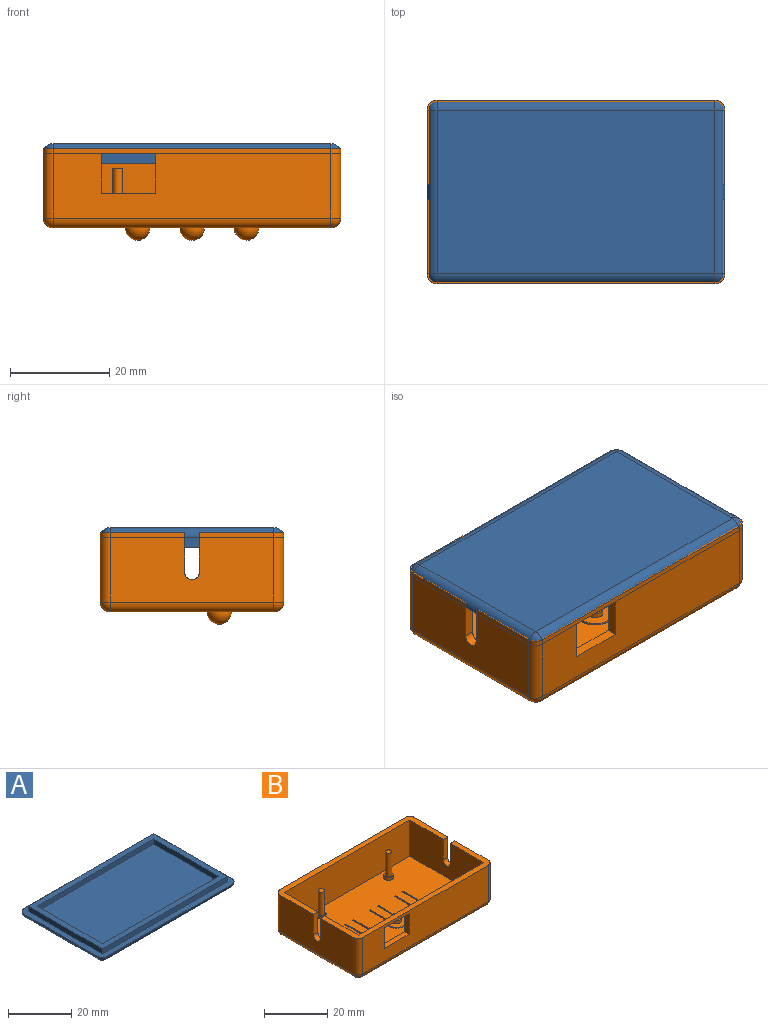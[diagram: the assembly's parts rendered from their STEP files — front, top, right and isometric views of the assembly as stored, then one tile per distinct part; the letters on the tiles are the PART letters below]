
ASSEMBLY  parts=2 mates=1
PART A: 20 faces, bbox 60x37x4 mm
  f0: plane 56x33mm, normal (0,0,1), area 340mm2, adj f3,f4,f5,f6,f8,f9,f10,f11
  f1: plane 60x37mm, normal (0,0,1), area 368.6mm2, adj f3,f4,f5,f6,f12,f13,f14,f15
  f2: plane 56x33mm, normal (0,0,-1), area 1848mm2, adj f13,f14,f17,f18
  f3: plane 33x2mm, normal (-1,0,0), area 66mm2, adj f0,f1,f4,f6
  f4: plane 56x2mm, normal (0,-1,0), area 112mm2, adj f0,f1,f3,f5
  f5: plane 33x2mm, normal (1,0,0), area 66mm2, adj f0,f1,f4,f6
  f6: plane 56x2mm, normal (0,1,0), area 112mm2, adj f0,f1,f3,f5
  f7: plane 52x29mm, normal (0,0,1), area 1508mm2, adj f8,f9,f10,f11
  f8: plane 29x2mm, normal (1,0,0), area 58mm2, adj f0,f7,f9,f11
  f9: plane 52x2mm, normal (0,1,0), area 104mm2, adj f0,f7,f8,f10
  f10: plane 29x2mm, normal (-1,0,0), area 58mm2, adj f0,f7,f9,f11
  f11: plane 52x2mm, normal (0,-1,0), area 104mm2, adj f0,f7,f8,f10
  f12: sphere r=2mm, area 6.3mm2, adj f1,f13,f14
  f13: cylinder r=2mm len=33mm, axis (0,1,0), area 103.7mm2, adj f1,f2,f12,f15
  f14: cylinder r=2mm len=56mm, axis (-1,0,0), area 175.9mm2, adj f1,f2,f12,f16
  f15: sphere r=2mm, area 6.3mm2, adj f1,f13,f17
  f16: sphere r=2mm, area 6.3mm2, adj f1,f14,f18
  f17: cylinder r=2mm len=56mm, axis (1,0,0), area 175.9mm2, adj f1,f2,f15,f19
  f18: cylinder r=2mm len=33mm, axis (0,-1,0), area 103.7mm2, adj f1,f2,f16,f19
  f19: sphere r=2mm, area 6.3mm2, adj f1,f17,f18
PART B: 79 faces, bbox 60x37x18.5 mm
  f0: plane 56x33mm, normal (0,0,1), area 1755.7mm2, adj f3,f9,f10,f11,f34,f35,f36,f37
  f1: plane 56x33mm, normal (0,0,-1), area 1739.2mm2, adj f15,f16,f20,f21,f34,f35,f36,f37
  f2: plane 56x14mm, normal (0,-1,0), area 696mm2, adj f7,f14,f20,f23,f30,f31,f32,f33
  f3: plane 56x14mm, normal (0,1,0), area 696mm2, adj f0,f7,f9,f10,f30,f31,f32,f33
  f4: plane 60x17mm, normal (0,0,1), area 178.3mm2, adj f5,f6,f8,f9,f10,f11,f12,f17
  f5: plane 33x14mm, normal (-1,0,0), area 434.5mm2, adj f4,f7,f17,f21,f23,f27,f28,f29
  f6: plane 33x14mm, normal (1,0,0), area 434.5mm2, adj f4,f7,f12,f14,f15,f24,f25,f26
  f7: plane 60x17mm, normal (0,0,1), area 178.3mm2, adj f2,f3,f5,f6,f9,f10,f14,f23
  f8: plane 56x14mm, normal (0,1,0), area 784mm2, adj f4,f12,f16,f17
  f9: plane 33x14mm, normal (1,0,0), area 434.5mm2, adj f0,f3,f4,f7,f11,f27,f28,f29
  f10: plane 33x14mm, normal (-1,0,0), area 434.5mm2, adj f0,f3,f4,f7,f11,f24,f25,f26
  f11: plane 56x14mm, normal (0,-1,0), area 784mm2, adj f0,f4,f9,f10
  f12: cylinder r=2mm len=14mm, axis (0,0,1), area 44mm2, adj f4,f6,f8,f13
  f13: sphere r=2mm, area 6.3mm2, adj f12,f15,f16
  f14: cylinder r=2mm len=14mm, axis (0,0,-1), area 44mm2, adj f2,f6,f7,f18
  f15: cylinder r=2mm len=33mm, axis (0,1,0), area 103.7mm2, adj f1,f6,f13,f18
  f16: cylinder r=2mm len=56mm, axis (-1,0,0), area 175.9mm2, adj f1,f8,f13,f19
  f17: cylinder r=2mm len=14mm, axis (0,0,-1), area 44mm2, adj f4,f5,f8,f19
  f18: sphere r=2mm, area 6.3mm2, adj f14,f15,f20
  f19: sphere r=2mm, area 6.3mm2, adj f16,f17,f21
  f20: cylinder r=2mm len=56mm, axis (1,0,0), area 175.9mm2, adj f1,f2,f18,f22
  f21: cylinder r=2mm len=33mm, axis (0,-1,0), area 103.7mm2, adj f1,f5,f19,f22
  f22: sphere r=2mm, area 6.3mm2, adj f20,f21,f23
  f23: cylinder r=2mm len=14mm, axis (0,0,1), area 44mm2, adj f2,f5,f7,f22
  f24: plane 8x2mm, normal (0,-1,0), area 16mm2, adj f4,f6,f10,f25
  f25: cylinder r=1.5mm len=3mm, axis (1,0,0), area 9.4mm2, adj f6,f10,f24,f26
  f26: plane 8x2mm, normal (0,1,0), area 16mm2, adj f6,f7,f10,f25
  f27: plane 8x2mm, normal (0,1,0), area 16mm2, adj f5,f7,f9,f28
  f28: cylinder r=1.5mm len=3mm, axis (1,0,0), area 9.4mm2, adj f5,f9,f27,f29
  f29: plane 8x2mm, normal (0,-1,0), area 16mm2, adj f4,f5,f9,f28
  f30: plane 11x2mm, normal (0,0,-1), area 22mm2, adj f2,f3,f31,f33
  f31: plane 8x2mm, normal (-1,0,0), area 16mm2, adj f2,f3,f30,f32
  f32: plane 11x2mm, normal (0,0,1), area 22mm2, adj f2,f3,f31,f33
  f33: plane 8x2mm, normal (1,0,0), area 16mm2, adj f2,f3,f30,f32
  f34: plane 6.84x2mm, normal (-1,0,0), area 13.7mm2, adj f0,f1,f35,f41
  f35: cylinder r=3.5mm len=7mm, axis (0,0,-1), area 37.8mm2, adj f0,f1,f34,f36
  f36: plane 6.84x2mm, normal (1,0,0), area 13.7mm2, adj f0,f1,f35,f37
  f37: plane 2x0.5mm, normal (0,-1,0), area 1mm2, adj f0,f1,f36,f38
  f38: plane 6.54x2mm, normal (-1,0,0), area 13.1mm2, adj f0,f1,f37,f39
  f39: cylinder r=4mm len=8mm, axis (0,0,-1), area 41.9mm2, adj f0,f1,f38,f40
  f40: plane 6.54x2mm, normal (1,0,0), area 13.1mm2, adj f0,f1,f39,f41
  f41: plane 2x0.5mm, normal (0,-1,0), area 1mm2, adj f0,f1,f34,f40
  f42: plane 6.84x2mm, normal (-1,0,0), area 13.7mm2, adj f0,f1,f43,f49
  f43: cylinder r=3.5mm len=7mm, axis (0,0,-1), area 37.8mm2, adj f0,f1,f42,f44
  f44: plane 6.84x2mm, normal (1,0,0), area 13.7mm2, adj f0,f1,f43,f45
  f45: plane 2x0.5mm, normal (0,-1,0), area 1mm2, adj f0,f1,f44,f46
  f46: plane 6.54x2mm, normal (-1,0,0), area 13.1mm2, adj f0,f1,f45,f47
  f47: cylinder r=4mm len=8mm, axis (0,0,-1), area 41.9mm2, adj f0,f1,f46,f48
  f48: plane 6.54x2mm, normal (1,0,0), area 13.1mm2, adj f0,f1,f47,f49
  f49: plane 2x0.5mm, normal (0,-1,0), area 1mm2, adj f0,f1,f42,f48
  f50: plane 6.84x2mm, normal (-1,0,0), area 13.7mm2, adj f0,f1,f51,f57
  f51: cylinder r=3.5mm len=7mm, axis (0,0,-1), area 37.8mm2, adj f0,f1,f50,f52
  f52: plane 6.84x2mm, normal (1,0,0), area 13.7mm2, adj f0,f1,f51,f53
  f53: plane 2x0.5mm, normal (0,-1,0), area 1mm2, adj f0,f1,f52,f54
  f54: plane 6.54x2mm, normal (-1,0,0), area 13.1mm2, adj f0,f1,f53,f55
  f55: cylinder r=4mm len=8mm, axis (0,0,-1), area 41.9mm2, adj f0,f1,f54,f56
  f56: plane 6.54x2mm, normal (1,0,0), area 13.1mm2, adj f0,f1,f55,f57
  f57: plane 2x0.5mm, normal (0,-1,0), area 1mm2, adj f0,f1,f50,f56
  f58: cylinder r=1.5mm len=3mm, axis (0,0,-1), area 9.4mm2, adj f0,f59
  f59: plane 3x3mm, normal (0,0,1), area 3.9mm2, adj f58,f61
  f60: plane 2x2mm, normal (0,0,1), area 3.1mm2, adj f61
  f61: cylinder r=1mm len=9mm, axis (0,0,-1), area 56.5mm2, adj f59,f60
  f62: cylinder r=1.5mm len=3mm, axis (0,0,-1), area 9.4mm2, adj f0,f63
  f63: plane 3x3mm, normal (0,0,1), area 3.9mm2, adj f62,f65
  f64: plane 2x2mm, normal (0,0,1), area 3.1mm2, adj f65
  f65: cylinder r=1mm len=9mm, axis (0,0,-1), area 56.5mm2, adj f63,f64
  f66: cylinder r=1.5mm len=3mm, axis (0,0,-1), area 9.4mm2, adj f0,f67
  f67: plane 3x3mm, normal (0,0,1), area 3.9mm2, adj f66,f69
  f68: plane 2x2mm, normal (0,0,1), area 3.1mm2, adj f69
  f69: cylinder r=1mm len=9mm, axis (0,0,-1), area 56.5mm2, adj f67,f68
  f70: cylinder r=1.5mm len=3mm, axis (0,0,-1), area 9.4mm2, adj f0,f71
  f71: plane 3x3mm, normal (0,0,1), area 7.1mm2, adj f70
  f72: cylinder r=1.5mm len=3mm, axis (0,0,-1), area 9.4mm2, adj f0,f73
  f73: plane 3x3mm, normal (0,0,1), area 7.1mm2, adj f72
  f74: cylinder r=1.5mm len=3mm, axis (0,0,-1), area 9.4mm2, adj f0,f75
  f75: plane 3x3mm, normal (0,0,1), area 7.1mm2, adj f74
  f76: sphere r=2.5mm, area 39.3mm2, adj f1
  f77: sphere r=2.5mm, area 39.3mm2, adj f1
  f78: sphere r=2.5mm, area 39.3mm2, adj f1
PLACE A rot(axis=(1,0,0),180deg) t=(-1.35,31.24,5.91)mm
PLACE B t=(-1.35,-5.76,-11.09)mm
MATE fastened A.f4 <-> B.f11  axis (0,1,0) through (28.65,29.24,2.91)mm
